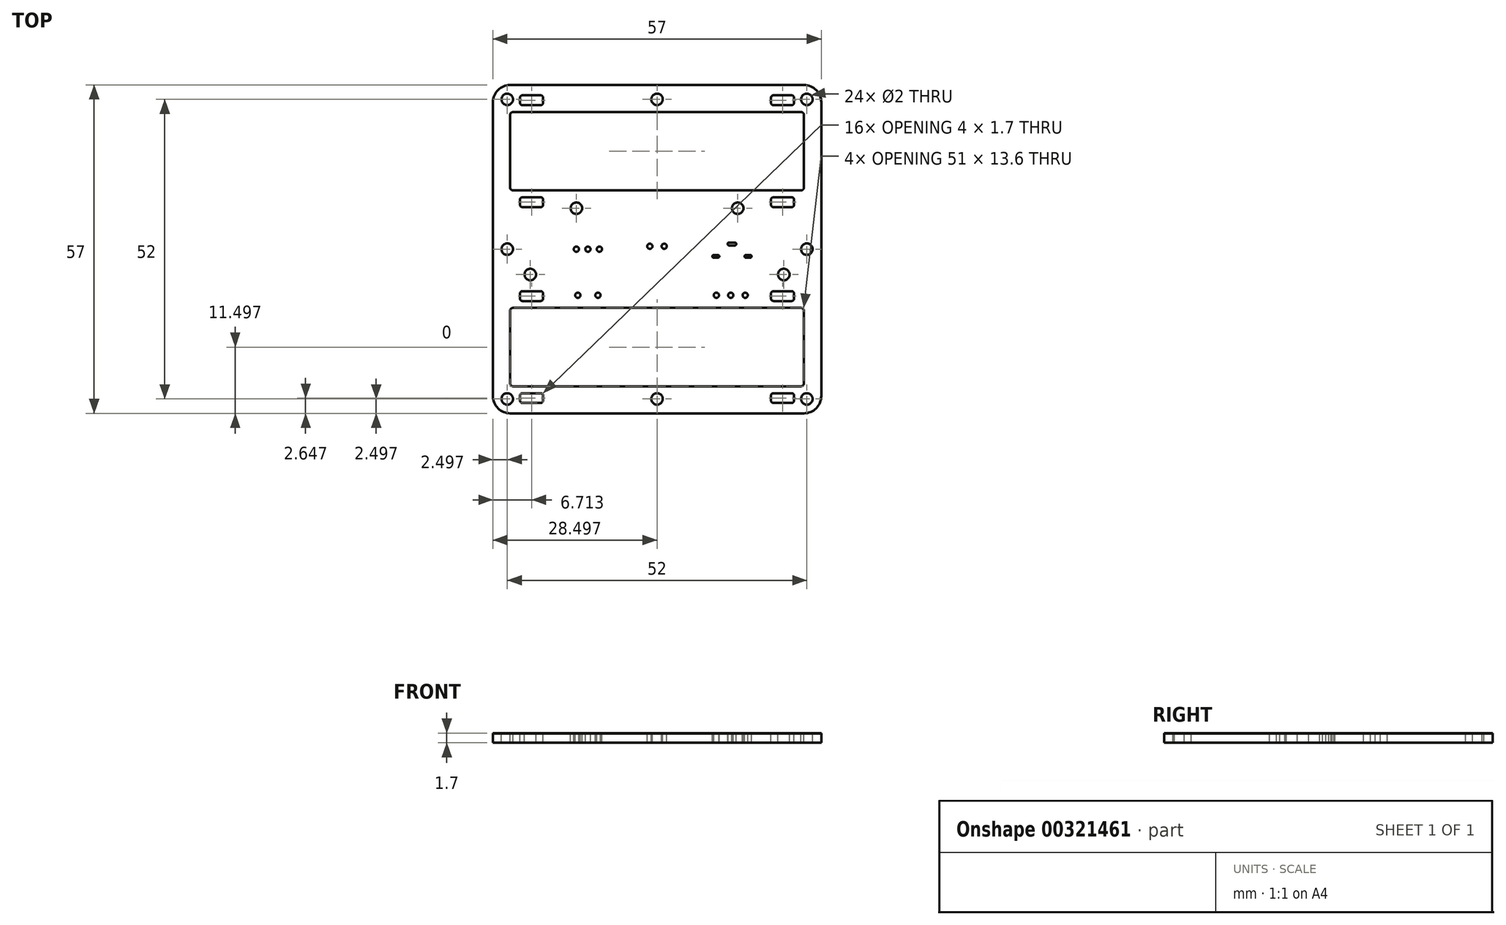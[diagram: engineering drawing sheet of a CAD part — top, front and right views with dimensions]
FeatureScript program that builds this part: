
annotation { "Feature Type Name" : "Feature", "Feature Type Description" : "" }
export const myFeature = defineFeature(function(context is Context, id is Id, definition is map)
    precondition{}
    {
        {
            var Q0;
            Q0=qCreatedBy(makeId("Top.planeOp"),FACE);
            var sketch = newSketch(context, id + "F0", { "sketchPlane" : qUnion([Q0])});
            skLineSegment(sketch, "E0.bottom", {"start": v(24.47, 58.7) * mm, "end": v(66.84, 58.7) * mm, "construction": true});
            skLineSegment(sketch, "E1.bottom", {"start": v(12.82, 58.7) * mm, "end": v(69.82, 58.7) * mm});
            skLineSegment(sketch, "E1.top", {"start": v(12.82, 1.7) * mm, "end": v(69.82, 1.7) * mm});
            skLineSegment(sketch, "E1.left", {"start": v(12.82, 58.7) * mm, "end": v(12.82, 1.7) * mm});
            skLineSegment(sketch, "E1.right", {"start": v(69.82, 58.7) * mm, "end": v(69.82, 1.7) * mm});
            skLineSegment(sketch, "E2", {"start": v(41.32, 58.7) * mm, "end": v(41.32, 1.7) * mm, "construction": true});
            skSolve(sketch);
        }
        {
            var Q0;
            Q0=qSketchRegion(id+"F0",true);
            extrude(context, id + "F1", {"entities" : qUnion([Q0]), "depth" : 1.6 * mm});
        }
        {
            var Q0;
            Q0=makeQuery(id+"F1.opExtrude","CAP_FACE",FACE,{"disambiguationData":[OSD([sQuery(id+"F0.wireOp",EDGE,"E1.bottom"),sQuery(id+"F0.wireOp",EDGE,"E1.top"),sQuery(id+"F0.wireOp",EDGE,"E1.left"),sQuery(id+"F0.wireOp",EDGE,"E1.right")])],"isStart":false});
            var sketch = newSketch(context, id + "F2", { "sketchPlane" : qUnion([Q0])});
            skCircle(sketch, "E3", {"center": v(27.32, 30.2) * mm, "radius": 0.45 * mm});
            skLineSegment(sketch, "E4", {"start": v(41.32, 22.32) * mm, "end": v(41.32, 29.29) * mm, "construction": true});
            skCircle(sketch, "E5.1.0.0", {"center": v(29.32, 30.2) * mm, "radius": 0.45 * mm});
            skLineSegment(sketch, "E5.direction1", {"start": v(27.32, 30.2) * mm, "end": v(29.32, 30.2) * mm, "construction": true});
            skCircle(sketch, "E6.0.2.0", {"center": v(31.32, 30.2) * mm, "radius": 0.45 * mm});
            skSolve(sketch);
        }
        {
            var Q0;
            Q0=makeQuery(id+"F1.opExtrude","CAP_FACE",FACE,{"disambiguationData":[OSD([sQuery(id+"F0.wireOp",EDGE,"E1.bottom"),sQuery(id+"F0.wireOp",EDGE,"E1.top"),sQuery(id+"F0.wireOp",EDGE,"E1.left"),sQuery(id+"F0.wireOp",EDGE,"E1.right")])],"isStart":false});
            var sketch = newSketch(context, id + "F3", { "sketchPlane" : qUnion([Q0])});
            skLineSegment(sketch, "E7", {"start": v(54.32, 14.1) * mm, "end": v(54.32, 27.42) * mm, "construction": true});
            skLineSegment(sketch, "E8", {"start": v(41.32, 6.29) * mm, "end": v(41.32, 24.04) * mm, "construction": true});
            skLineSegment(sketch, "E9", {"start": v(51.17, 28.95) * mm, "end": v(51.87, 28.95) * mm, "construction": true});
            skLineSegment(sketch, "E10", {"start": v(51.52, 23.97) * mm, "end": v(51.52, 28.95) * mm, "construction": true});
            skLineSegment(sketch, "E11", {"start": v(53.82, 31.1) * mm, "end": v(54.82, 31.1) * mm, "construction": true});
            skLineSegment(sketch, "E12", {"start": v(54.32, 31.1) * mm, "end": v(54.32, 19.92) * mm, "construction": true});
            skArc(sketch, "E13.0.startCap", {"start": v(53.82, 30.85) * mm, "mid": v(53.57, 31.1) * mm, "end": v(53.82, 31.35) * mm});
            skArc(sketch, "E13.0.endCap", {"start": v(54.82, 31.35) * mm, "mid": v(55.07, 31.1) * mm, "end": v(54.82, 30.85) * mm});
            skLineSegment(sketch, "E13.0.left", {"start": v(53.82, 31.35) * mm, "end": v(54.82, 31.35) * mm});
            skLineSegment(sketch, "E13.0.right", {"start": v(53.82, 30.85) * mm, "end": v(54.82, 30.85) * mm});
            skLineSegment(sketch, "E14", {"start": v(50.45, 30.1) * mm, "end": v(53.65, 30.1) * mm, "construction": true});
            skArc(sketch, "E15.0.startCap", {"start": v(51.87, 29.2) * mm, "mid": v(52.12, 28.95) * mm, "end": v(51.87, 28.7) * mm});
            skArc(sketch, "E15.0.endCap", {"start": v(51.17, 28.7) * mm, "mid": v(50.92, 28.95) * mm, "end": v(51.17, 29.2) * mm});
            skLineSegment(sketch, "E15.0.left", {"start": v(51.17, 28.7) * mm, "end": v(51.87, 28.7) * mm});
            skLineSegment(sketch, "E15.0.right", {"start": v(51.17, 29.2) * mm, "end": v(51.87, 29.2) * mm});
            skArc(sketch, "E16.MirrorCS", {"start": v(57.47, 28.7) * mm, "mid": v(57.72, 28.95) * mm, "end": v(57.47, 29.2) * mm});
            skLineSegment(sketch, "E17.MirrorCS", {"start": v(57.47, 28.7) * mm, "end": v(56.77, 28.7) * mm});
            skLineSegment(sketch, "E18.MirrorCS", {"start": v(57.47, 29.2) * mm, "end": v(56.77, 29.2) * mm});
            skArc(sketch, "E19.MirrorCS", {"start": v(56.77, 29.2) * mm, "mid": v(56.52, 28.95) * mm, "end": v(56.77, 28.7) * mm});
            skSolve(sketch);
        }
        {
            var Q0;
            Q0=makeQuery(id+"F1.opExtrude","CAP_FACE",FACE,{"disambiguationData":[OSD([sQuery(id+"F0.wireOp",EDGE,"E1.bottom"),sQuery(id+"F0.wireOp",EDGE,"E1.top"),sQuery(id+"F0.wireOp",EDGE,"E1.left"),sQuery(id+"F0.wireOp",EDGE,"E1.right")])],"isStart":false});
            var sketch = newSketch(context, id + "F4", { "sketchPlane" : qUnion([Q0])});
            skCircle(sketch, "E20", {"center": v(51.62, 22.2) * mm, "radius": 0.45 * mm});
            skCircle(sketch, "E21.1.0.0", {"center": v(56.62, 22.2) * mm, "radius": 0.45 * mm});
            skLineSegment(sketch, "E21.direction1", {"start": v(51.62, 22.2) * mm, "end": v(56.62, 22.2) * mm, "construction": true});
            skLineSegment(sketch, "E22", {"start": v(41.32, 6.29) * mm, "end": v(41.32, 17.65) * mm, "construction": true});
            skLineSegment(sketch, "E23", {"start": v(54.12, 22.2) * mm, "end": v(54.12, 23.7) * mm, "construction": true});
            skCircle(sketch, "E24", {"center": v(54.12, 22.2) * mm, "radius": 0.45 * mm});
            skSolve(sketch);
        }
        {
            var Q0;
            Q0=makeQuery(id+"F1.opExtrude","CAP_FACE",FACE,{"disambiguationData":[OSD([sQuery(id+"F0.wireOp",EDGE,"E1.bottom"),sQuery(id+"F0.wireOp",EDGE,"E1.top"),sQuery(id+"F0.wireOp",EDGE,"E1.left"),sQuery(id+"F0.wireOp",EDGE,"E1.right")])],"isStart":false});
            var sketch = newSketch(context, id + "F5", { "sketchPlane" : qUnion([Q0])});
            skCircle(sketch, "E25", {"center": v(40.07, 30.7) * mm, "radius": 0.45 * mm});
            skCircle(sketch, "E26.1.0.0", {"center": v(42.57, 30.7) * mm, "radius": 0.45 * mm});
            skLineSegment(sketch, "E26.direction1", {"start": v(40.07, 30.7) * mm, "end": v(42.57, 30.7) * mm, "construction": true});
            skLineSegment(sketch, "E27", {"start": v(41.32, 15.29) * mm, "end": v(41.32, 29.29) * mm, "construction": true});
            skLineSegment(sketch, "E28", {"start": v(41.32, 26.14) * mm, "end": v(41.32, 30.7) * mm, "construction": true});
            skSolve(sketch);
        }
        {
            var Q0;
            Q0=makeQuery(id+"F1.opExtrude","CAP_FACE",FACE,{"disambiguationData":[OSD([sQuery(id+"F0.wireOp",EDGE,"E1.bottom"),sQuery(id+"F0.wireOp",EDGE,"E1.top"),sQuery(id+"F0.wireOp",EDGE,"E1.left"),sQuery(id+"F0.wireOp",EDGE,"E1.right")])],"isStart":false});
            var sketch = newSketch(context, id + "F6", { "sketchPlane" : qUnion([Q0])});
            skCircle(sketch, "E29", {"center": v(27.57, 22.2) * mm, "radius": 0.45 * mm});
            skCircle(sketch, "E30.1.0.0", {"center": v(31.07, 22.2) * mm, "radius": 0.45 * mm});
            skLineSegment(sketch, "E30.direction1", {"start": v(27.57, 22.2) * mm, "end": v(31.07, 22.2) * mm, "construction": true});
            skLineSegment(sketch, "E31", {"start": v(29.32, 26.4) * mm, "end": v(29.32, 22.2) * mm, "construction": true});
            skSolve(sketch);
        }
        {
            var Q0;
            Q0=qSketchRegion(id+"F4",true);
            var Q1;
            Q1=qSketchRegion(id+"F5",true);
            var Q2;
            Q2=qSketchRegion(id+"F6",true);
            var Q3;
            Q3=qSketchRegion(id+"F3",true);
            var Q4;
            Q4=qSketchRegion(id+"F2",true);
            extrude(context, id + "F7", {"entities" : qUnion([Q0, Q1, Q2, Q3, Q4]), "operationType" : NewBodyOperationType.REMOVE, "oppositeDirection" : true, "depth" : 4 * mm});
        }
        {
            var Q0;
            Q0=makeQuery(id+"F1.opExtrude","SWEPT_EDGE",EDGE,{"disambiguationData":[OSD([sQuery(id+"F0.wireOp",EDGE,"E1.top"),sQuery(id+"F0.wireOp",EDGE,"E1.left")])]});
            var Q1;
            Q1=makeQuery(id+"F1.opExtrude","SWEPT_EDGE",EDGE,{"disambiguationData":[OSD([sQuery(id+"F0.wireOp",EDGE,"E1.top"),sQuery(id+"F0.wireOp",EDGE,"E1.right")])]});
            var Q2;
            Q2=makeQuery(id+"F1.opExtrude","SWEPT_EDGE",EDGE,{"disambiguationData":[OSD([sQuery(id+"F0.wireOp",EDGE,"E1.bottom"),sQuery(id+"F0.wireOp",EDGE,"E1.right")])]});
            var Q3;
            Q3=makeQuery(id+"F1.opExtrude","SWEPT_EDGE",EDGE,{"disambiguationData":[OSD([sQuery(id+"F0.wireOp",EDGE,"E1.bottom"),sQuery(id+"F0.wireOp",EDGE,"E1.left")])]});
            fillet(context, id + "F8", {"entities" : qUnion([Q0, Q1, Q2, Q3]), "radius" : 3 * mm, "tangentPropagation" : true, "allowEdgeOverflow" : false});
        }
        {
            var Q0;
            Q0=makeQuery(id+"F1.opExtrude","CAP_FACE",FACE,{"disambiguationData":[OSD([sQuery(id+"F0.wireOp",EDGE,"E1.bottom"),sQuery(id+"F0.wireOp",EDGE,"E1.top"),sQuery(id+"F0.wireOp",EDGE,"E1.left"),sQuery(id+"F0.wireOp",EDGE,"E1.right")])],"isStart":false});
            var sketch = newSketch(context, id + "F9", { "sketchPlane" : qUnion([Q0])});
            skLineSegment(sketch, "E32", {"start": v(41.32, 58.7) * mm, "end": v(41.32, 1.7) * mm, "construction": true});
            skLineSegment(sketch, "E33", {"start": v(12.82, 30.2) * mm, "end": v(69.82, 30.2) * mm, "construction": true});
            skCircle(sketch, "E34", {"center": v(63.32, 25.8) * mm, "radius": 1 * mm});
            skCircle(sketch, "E35.MirrorC", {"center": v(19.32, 25.8) * mm, "radius": 1 * mm});
            skCircle(sketch, "E36", {"center": v(55.32, 37.3) * mm, "radius": 1 * mm});
            skCircle(sketch, "E37.MirrorC", {"center": v(27.32, 37.3) * mm, "radius": 1 * mm});
            skCircle(sketch, "E38", {"center": v(15.32, 56.2) * mm, "radius": 1 * mm});
            skCircle(sketch, "E39.MirrorC", {"center": v(67.32, 56.2) * mm, "radius": 1 * mm});
            skCircle(sketch, "E40.MirrorC", {"center": v(15.32, 4.2) * mm, "radius": 1 * mm});
            skCircle(sketch, "E41.MirrorC", {"center": v(67.32, 4.2) * mm, "radius": 1 * mm});
            skCircle(sketch, "E42", {"center": v(41.32, 56.2) * mm, "radius": 1 * mm});
            skCircle(sketch, "E43.MirrorC", {"center": v(41.32, 4.2) * mm, "radius": 1 * mm});
            skCircle(sketch, "E44", {"center": v(15.32, 30.2) * mm, "radius": 1 * mm});
            skCircle(sketch, "E45", {"center": v(67.32, 30.2) * mm, "radius": 1 * mm});
            skSolve(sketch);
        }
        {
            var Q0;
            Q0=qSketchRegion(id+"F9",true);
            extrude(context, id + "F10", {"entities" : qUnion([Q0]), "operationType" : NewBodyOperationType.REMOVE, "oppositeDirection" : true, "depth" : 25 * mm});
        }
        {
            var Q0;
            Q0=makeQuery(id+"F1.opExtrude","CAP_FACE",FACE,{"disambiguationData":[OSD([sQuery(id+"F0.wireOp",EDGE,"E1.bottom"),sQuery(id+"F0.wireOp",EDGE,"E1.top"),sQuery(id+"F0.wireOp",EDGE,"E1.left"),sQuery(id+"F0.wireOp",EDGE,"E1.right")])],"isStart":false});
            var sketch = newSketch(context, id + "F11", { "sketchPlane" : qUnion([Q0])});
            skLineSegment(sketch, "E46", {"start": v(41.32, 58.7) * mm, "end": v(41.32, 1.7) * mm, "construction": true});
            skLineSegment(sketch, "E47.bottom", {"start": v(66.32, 20) * mm, "end": v(16.32, 20) * mm});
            skLineSegment(sketch, "E47.top", {"start": v(66.32, 6.4) * mm, "end": v(16.32, 6.4) * mm});
            skLineSegment(sketch, "E47.left", {"start": v(66.82, 19.5) * mm, "end": v(66.82, 6.9) * mm});
            skLineSegment(sketch, "E47.right", {"start": v(15.82, 19.5) * mm, "end": v(15.82, 6.9) * mm});
            skPoint(sketch, "E47.middle", {"position": v(41.32, 13.2) * mm});
            skLineSegment(sketch, "E48", {"start": v(41.32, 30.2) * mm, "end": v(-6.1, 30.2) * mm, "construction": true});
            skPoint(sketch, "E49.visualSharp", {"position": v(15.82, 6.4) * mm});
            skArc(sketch, "E49.filletArc", {"start": v(15.82, 6.9) * mm, "mid": v(15.96, 6.54) * mm, "end": v(16.32, 6.4) * mm});
            skPoint(sketch, "E50.visualSharp", {"position": v(15.82, 20) * mm});
            skArc(sketch, "E50.filletArc", {"start": v(16.32, 20) * mm, "mid": v(15.96, 19.85) * mm, "end": v(15.82, 19.5) * mm});
            skPoint(sketch, "E51.visualSharp", {"position": v(66.82, 20) * mm});
            skArc(sketch, "E51.filletArc", {"start": v(66.82, 19.5) * mm, "mid": v(66.67, 19.85) * mm, "end": v(66.32, 20) * mm});
            skPoint(sketch, "E52.visualSharp", {"position": v(66.82, 6.4) * mm});
            skArc(sketch, "E52.filletArc", {"start": v(66.32, 6.4) * mm, "mid": v(66.67, 6.54) * mm, "end": v(66.82, 6.9) * mm});
            skArc(sketch, "E53.MirrorCS", {"start": v(15.82, 53.5) * mm, "mid": v(15.96, 53.85) * mm, "end": v(16.32, 54) * mm});
            skArc(sketch, "E54.MirrorCS", {"start": v(16.32, 40.4) * mm, "mid": v(15.96, 40.54) * mm, "end": v(15.82, 40.9) * mm});
            skArc(sketch, "E55.MirrorCS", {"start": v(66.82, 40.9) * mm, "mid": v(66.67, 40.54) * mm, "end": v(66.32, 40.4) * mm});
            skArc(sketch, "E56.MirrorCS", {"start": v(66.32, 54) * mm, "mid": v(66.67, 53.85) * mm, "end": v(66.82, 53.5) * mm});
            skLineSegment(sketch, "E57.MirrorCS", {"start": v(15.82, 40.9) * mm, "end": v(15.82, 53.5) * mm});
            skLineSegment(sketch, "E58.MirrorCS", {"start": v(66.32, 40.4) * mm, "end": v(16.32, 40.4) * mm});
            skLineSegment(sketch, "E59.MirrorCS", {"start": v(66.82, 40.9) * mm, "end": v(66.82, 53.5) * mm});
            skLineSegment(sketch, "E60.MirrorCS", {"start": v(66.32, 54) * mm, "end": v(16.32, 54) * mm});
            skPoint(sketch, "E61.MirrorP", {"position": v(66.82, 54) * mm});
            skPoint(sketch, "E62.MirrorP", {"position": v(15.82, 54) * mm});
            skPoint(sketch, "E63.MirrorP", {"position": v(41.32, 47.2) * mm});
            skPoint(sketch, "E64.MirrorP", {"position": v(66.82, 40.4) * mm});
            skPoint(sketch, "E65.MirrorP", {"position": v(15.82, 40.4) * mm});
            skSolve(sketch);
        }
        {
            var Q0;
            Q0=qSketchRegion(id+"F11",true);
            extrude(context, id + "F12", {"entities" : qUnion([Q0]), "operationType" : NewBodyOperationType.REMOVE, "oppositeDirection" : true, "depth" : 5 * mm});
        }
        {
            var Q0;
            Q0=makeQuery(id+"F1.opExtrude","CAP_FACE",FACE,{"disambiguationData":[OSD([sQuery(id+"F0.wireOp",EDGE,"E1.bottom"),sQuery(id+"F0.wireOp",EDGE,"E1.top"),sQuery(id+"F0.wireOp",EDGE,"E1.left"),sQuery(id+"F0.wireOp",EDGE,"E1.right")])],"isStart":false});
            var sketch = newSketch(context, id + "F13", { "sketchPlane" : qUnion([Q0])});
            skLineSegment(sketch, "E66.bottom", {"start": v(17.53, 5.2) * mm, "end": v(21.53, 5.2) * mm});
            skLineSegment(sketch, "E66.top", {"start": v(17.53, 3.5) * mm, "end": v(21.53, 3.5) * mm});
            skLineSegment(sketch, "E66.left", {"start": v(17.53, 5.2) * mm, "end": v(17.53, 3.5) * mm});
            skLineSegment(sketch, "E66.right", {"start": v(21.53, 5.2) * mm, "end": v(21.53, 3.5) * mm});
            skLineSegment(sketch, "E67.MirrorCS", {"start": v(65.1, 5.2) * mm, "end": v(65.1, 3.5) * mm});
            skLineSegment(sketch, "E68.MirrorCS", {"start": v(61.1, 5.2) * mm, "end": v(61.1, 3.5) * mm});
            skLineSegment(sketch, "E69.MirrorCS", {"start": v(65.1, 3.5) * mm, "end": v(61.1, 3.5) * mm});
            skLineSegment(sketch, "E70.MirrorCS", {"start": v(65.1, 5.2) * mm, "end": v(61.1, 5.2) * mm});
            skLineSegment(sketch, "E71", {"start": v(12.82, 30.2) * mm, "end": v(83.5, 30.2) * mm, "construction": true});
            skLineSegment(sketch, "E72", {"start": v(15.82, 13.2) * mm, "end": v(-2.11, 13.2) * mm, "construction": true});
            skPoint(sketch, "E72.endSnap0", {"position": v(15.82, 13.2) * mm});
            skLineSegment(sketch, "E73.MirrorCS", {"start": v(61.1, 21.2) * mm, "end": v(61.1, 22.9) * mm});
            skLineSegment(sketch, "E74.MirrorCS", {"start": v(65.1, 21.2) * mm, "end": v(65.1, 22.9) * mm});
            skLineSegment(sketch, "E75.MirrorCS", {"start": v(21.53, 21.2) * mm, "end": v(21.53, 22.9) * mm});
            skLineSegment(sketch, "E76.MirrorCS", {"start": v(17.53, 21.2) * mm, "end": v(17.53, 22.9) * mm});
            skLineSegment(sketch, "E77.MirrorCS", {"start": v(65.1, 21.2) * mm, "end": v(61.1, 21.2) * mm});
            skLineSegment(sketch, "E78.MirrorCS", {"start": v(65.1, 22.9) * mm, "end": v(61.1, 22.9) * mm});
            skLineSegment(sketch, "E79.MirrorCS", {"start": v(17.53, 22.9) * mm, "end": v(21.53, 22.9) * mm});
            skLineSegment(sketch, "E80.MirrorCS", {"start": v(17.53, 21.2) * mm, "end": v(21.53, 21.2) * mm});
            skLineSegment(sketch, "E81.MirrorCS", {"start": v(17.53, 39.2) * mm, "end": v(17.53, 37.5) * mm});
            skLineSegment(sketch, "E82.MirrorCS", {"start": v(17.53, 55.2) * mm, "end": v(17.53, 56.9) * mm});
            skLineSegment(sketch, "E83.MirrorCS", {"start": v(61.1, 39.2) * mm, "end": v(61.1, 37.5) * mm});
            skLineSegment(sketch, "E84.MirrorCS", {"start": v(21.53, 55.2) * mm, "end": v(21.53, 56.9) * mm});
            skLineSegment(sketch, "E85.MirrorCS", {"start": v(65.1, 55.2) * mm, "end": v(65.1, 56.9) * mm});
            skLineSegment(sketch, "E86.MirrorCS", {"start": v(21.53, 39.2) * mm, "end": v(21.53, 37.5) * mm});
            skLineSegment(sketch, "E87.MirrorCS", {"start": v(61.1, 55.2) * mm, "end": v(61.1, 56.9) * mm});
            skLineSegment(sketch, "E88.MirrorCS", {"start": v(65.1, 39.2) * mm, "end": v(65.1, 37.5) * mm});
            skLineSegment(sketch, "E89.MirrorCS", {"start": v(17.53, 56.9) * mm, "end": v(21.53, 56.9) * mm});
            skLineSegment(sketch, "E90.MirrorCS", {"start": v(65.1, 39.2) * mm, "end": v(61.1, 39.2) * mm});
            skLineSegment(sketch, "E91.MirrorCS", {"start": v(65.1, 37.5) * mm, "end": v(61.1, 37.5) * mm});
            skLineSegment(sketch, "E92.MirrorCS", {"start": v(17.53, 39.2) * mm, "end": v(21.53, 39.2) * mm});
            skLineSegment(sketch, "E93.MirrorCS", {"start": v(17.53, 55.2) * mm, "end": v(21.53, 55.2) * mm});
            skLineSegment(sketch, "E94.MirrorCS", {"start": v(65.1, 56.9) * mm, "end": v(61.1, 56.9) * mm});
            skPoint(sketch, "E95.MirrorP", {"position": v(15.82, 47.2) * mm});
            skLineSegment(sketch, "E96.MirrorCS", {"start": v(65.1, 55.2) * mm, "end": v(61.1, 55.2) * mm});
            skLineSegment(sketch, "E97.MirrorCS", {"start": v(17.53, 37.5) * mm, "end": v(21.53, 37.5) * mm});
            skSolve(sketch);
        }
        {
            var Q0;
            Q0=qSketchRegion(id+"F13",true);
            extrude(context, id + "F14", {"entities" : qUnion([Q0]), "operationType" : NewBodyOperationType.REMOVE, "oppositeDirection" : true, "depth" : 25 * mm});
        }
        {
            var Q0;
            Q0=makeQuery(id+"F14.boolean.opBoolean","COPY",EDGE,{"derivedFrom":makeQuery(id+"F14.opExtrude","SWEPT_EDGE",EDGE,{"disambiguationData":[OSD([sQuery(id+"F13.wireOp",EDGE,"E82.MirrorCS"),sQuery(id+"F13.wireOp",EDGE,"E89.MirrorCS")])]})});
            var Q1;
            Q1=makeQuery(id+"F14.boolean.opBoolean","COPY",EDGE,{"derivedFrom":makeQuery(id+"F14.opExtrude","SWEPT_EDGE",EDGE,{"disambiguationData":[OSD([sQuery(id+"F13.wireOp",EDGE,"E82.MirrorCS"),sQuery(id+"F13.wireOp",EDGE,"E93.MirrorCS")])]})});
            var Q2;
            Q2=makeQuery(id+"F14.boolean.opBoolean","COPY",EDGE,{"derivedFrom":makeQuery(id+"F14.opExtrude","SWEPT_EDGE",EDGE,{"disambiguationData":[OSD([sQuery(id+"F13.wireOp",EDGE,"E84.MirrorCS"),sQuery(id+"F13.wireOp",EDGE,"E93.MirrorCS")])]})});
            var Q3;
            Q3=makeQuery(id+"F14.boolean.opBoolean","COPY",EDGE,{"derivedFrom":makeQuery(id+"F14.opExtrude","SWEPT_EDGE",EDGE,{"disambiguationData":[OSD([sQuery(id+"F13.wireOp",EDGE,"E84.MirrorCS"),sQuery(id+"F13.wireOp",EDGE,"E89.MirrorCS")])]})});
            var Q4;
            Q4=makeQuery(id+"F14.boolean.opBoolean","COPY",EDGE,{"derivedFrom":makeQuery(id+"F14.opExtrude","SWEPT_EDGE",EDGE,{"disambiguationData":[OSD([sQuery(id+"F13.wireOp",EDGE,"E86.MirrorCS"),sQuery(id+"F13.wireOp",EDGE,"E92.MirrorCS")])]})});
            var Q5;
            Q5=makeQuery(id+"F14.boolean.opBoolean","COPY",EDGE,{"derivedFrom":makeQuery(id+"F14.opExtrude","SWEPT_EDGE",EDGE,{"disambiguationData":[OSD([sQuery(id+"F13.wireOp",EDGE,"E81.MirrorCS"),sQuery(id+"F13.wireOp",EDGE,"E92.MirrorCS")])]})});
            var Q6;
            Q6=makeQuery(id+"F14.boolean.opBoolean","COPY",EDGE,{"derivedFrom":makeQuery(id+"F14.opExtrude","SWEPT_EDGE",EDGE,{"disambiguationData":[OSD([sQuery(id+"F13.wireOp",EDGE,"E81.MirrorCS"),sQuery(id+"F13.wireOp",EDGE,"E97.MirrorCS")])]})});
            var Q7;
            Q7=makeQuery(id+"F14.boolean.opBoolean","COPY",EDGE,{"derivedFrom":makeQuery(id+"F14.opExtrude","SWEPT_EDGE",EDGE,{"disambiguationData":[OSD([sQuery(id+"F13.wireOp",EDGE,"E86.MirrorCS"),sQuery(id+"F13.wireOp",EDGE,"E97.MirrorCS")])]})});
            var Q8;
            Q8=makeQuery(id+"F14.boolean.opBoolean","COPY",EDGE,{"derivedFrom":makeQuery(id+"F14.opExtrude","SWEPT_EDGE",EDGE,{"disambiguationData":[OSD([sQuery(id+"F13.wireOp",EDGE,"E85.MirrorCS"),sQuery(id+"F13.wireOp",EDGE,"E96.MirrorCS")])]})});
            var Q9;
            Q9=makeQuery(id+"F14.boolean.opBoolean","COPY",EDGE,{"derivedFrom":makeQuery(id+"F14.opExtrude","SWEPT_EDGE",EDGE,{"disambiguationData":[OSD([sQuery(id+"F13.wireOp",EDGE,"E85.MirrorCS"),sQuery(id+"F13.wireOp",EDGE,"E94.MirrorCS")])]})});
            var Q10;
            Q10=makeQuery(id+"F14.boolean.opBoolean","COPY",EDGE,{"derivedFrom":makeQuery(id+"F14.opExtrude","SWEPT_EDGE",EDGE,{"disambiguationData":[OSD([sQuery(id+"F13.wireOp",EDGE,"E87.MirrorCS"),sQuery(id+"F13.wireOp",EDGE,"E94.MirrorCS")])]})});
            var Q11;
            Q11=makeQuery(id+"F14.boolean.opBoolean","COPY",EDGE,{"derivedFrom":makeQuery(id+"F14.opExtrude","SWEPT_EDGE",EDGE,{"disambiguationData":[OSD([sQuery(id+"F13.wireOp",EDGE,"E87.MirrorCS"),sQuery(id+"F13.wireOp",EDGE,"E96.MirrorCS")])]})});
            var Q12;
            Q12=makeQuery(id+"F14.boolean.opBoolean","COPY",EDGE,{"derivedFrom":makeQuery(id+"F14.opExtrude","SWEPT_EDGE",EDGE,{"disambiguationData":[OSD([sQuery(id+"F13.wireOp",EDGE,"E83.MirrorCS"),sQuery(id+"F13.wireOp",EDGE,"E91.MirrorCS")])]})});
            var Q13;
            Q13=makeQuery(id+"F14.boolean.opBoolean","COPY",EDGE,{"derivedFrom":makeQuery(id+"F14.opExtrude","SWEPT_EDGE",EDGE,{"disambiguationData":[OSD([sQuery(id+"F13.wireOp",EDGE,"E83.MirrorCS"),sQuery(id+"F13.wireOp",EDGE,"E90.MirrorCS")])]})});
            var Q14;
            Q14=makeQuery(id+"F14.boolean.opBoolean","COPY",EDGE,{"derivedFrom":makeQuery(id+"F14.opExtrude","SWEPT_EDGE",EDGE,{"disambiguationData":[OSD([sQuery(id+"F13.wireOp",EDGE,"E88.MirrorCS"),sQuery(id+"F13.wireOp",EDGE,"E90.MirrorCS")])]})});
            var Q15;
            Q15=makeQuery(id+"F14.boolean.opBoolean","COPY",EDGE,{"derivedFrom":makeQuery(id+"F14.opExtrude","SWEPT_EDGE",EDGE,{"disambiguationData":[OSD([sQuery(id+"F13.wireOp",EDGE,"E88.MirrorCS"),sQuery(id+"F13.wireOp",EDGE,"E91.MirrorCS")])]})});
            var Q16;
            Q16=makeQuery(id+"F14.boolean.opBoolean","COPY",EDGE,{"derivedFrom":makeQuery(id+"F14.opExtrude","SWEPT_EDGE",EDGE,{"disambiguationData":[OSD([sQuery(id+"F13.wireOp",EDGE,"E75.MirrorCS"),sQuery(id+"F13.wireOp",EDGE,"E80.MirrorCS")])]})});
            var Q17;
            Q17=makeQuery(id+"F14.boolean.opBoolean","COPY",EDGE,{"derivedFrom":makeQuery(id+"F14.opExtrude","SWEPT_EDGE",EDGE,{"disambiguationData":[OSD([sQuery(id+"F13.wireOp",EDGE,"E75.MirrorCS"),sQuery(id+"F13.wireOp",EDGE,"E79.MirrorCS")])]})});
            var Q18;
            Q18=makeQuery(id+"F14.boolean.opBoolean","COPY",EDGE,{"derivedFrom":makeQuery(id+"F14.opExtrude","SWEPT_EDGE",EDGE,{"disambiguationData":[OSD([sQuery(id+"F13.wireOp",EDGE,"E76.MirrorCS"),sQuery(id+"F13.wireOp",EDGE,"E79.MirrorCS")])]})});
            var Q19;
            Q19=makeQuery(id+"F14.boolean.opBoolean","COPY",EDGE,{"derivedFrom":makeQuery(id+"F14.opExtrude","SWEPT_EDGE",EDGE,{"disambiguationData":[OSD([sQuery(id+"F13.wireOp",EDGE,"E76.MirrorCS"),sQuery(id+"F13.wireOp",EDGE,"E80.MirrorCS")])]})});
            var Q20;
            Q20=makeQuery(id+"F14.boolean.opBoolean","COPY",EDGE,{"derivedFrom":makeQuery(id+"F14.opExtrude","SWEPT_EDGE",EDGE,{"disambiguationData":[OSD([sQuery(id+"F13.wireOp",EDGE,"E73.MirrorCS"),sQuery(id+"F13.wireOp",EDGE,"E77.MirrorCS")])]})});
            var Q21;
            Q21=makeQuery(id+"F14.boolean.opBoolean","COPY",EDGE,{"derivedFrom":makeQuery(id+"F14.opExtrude","SWEPT_EDGE",EDGE,{"disambiguationData":[OSD([sQuery(id+"F13.wireOp",EDGE,"E73.MirrorCS"),sQuery(id+"F13.wireOp",EDGE,"E78.MirrorCS")])]})});
            var Q22;
            Q22=makeQuery(id+"F14.boolean.opBoolean","COPY",EDGE,{"derivedFrom":makeQuery(id+"F14.opExtrude","SWEPT_EDGE",EDGE,{"disambiguationData":[OSD([sQuery(id+"F13.wireOp",EDGE,"E74.MirrorCS"),sQuery(id+"F13.wireOp",EDGE,"E78.MirrorCS")])]})});
            var Q23;
            Q23=makeQuery(id+"F14.boolean.opBoolean","COPY",EDGE,{"derivedFrom":makeQuery(id+"F14.opExtrude","SWEPT_EDGE",EDGE,{"disambiguationData":[OSD([sQuery(id+"F13.wireOp",EDGE,"E74.MirrorCS"),sQuery(id+"F13.wireOp",EDGE,"E77.MirrorCS")])]})});
            var Q24;
            Q24=makeQuery(id+"F14.boolean.opBoolean","COPY",EDGE,{"derivedFrom":makeQuery(id+"F14.opExtrude","SWEPT_EDGE",EDGE,{"disambiguationData":[OSD([sQuery(id+"F13.wireOp",EDGE,"E67.MirrorCS"),sQuery(id+"F13.wireOp",EDGE,"E69.MirrorCS")])]})});
            var Q25;
            Q25=makeQuery(id+"F14.boolean.opBoolean","COPY",EDGE,{"derivedFrom":makeQuery(id+"F14.opExtrude","SWEPT_EDGE",EDGE,{"disambiguationData":[OSD([sQuery(id+"F13.wireOp",EDGE,"E67.MirrorCS"),sQuery(id+"F13.wireOp",EDGE,"E70.MirrorCS")])]})});
            var Q26;
            Q26=makeQuery(id+"F14.boolean.opBoolean","COPY",EDGE,{"derivedFrom":makeQuery(id+"F14.opExtrude","SWEPT_EDGE",EDGE,{"disambiguationData":[OSD([sQuery(id+"F13.wireOp",EDGE,"E68.MirrorCS"),sQuery(id+"F13.wireOp",EDGE,"E70.MirrorCS")])]})});
            var Q27;
            Q27=makeQuery(id+"F14.boolean.opBoolean","COPY",EDGE,{"derivedFrom":makeQuery(id+"F14.opExtrude","SWEPT_EDGE",EDGE,{"disambiguationData":[OSD([sQuery(id+"F13.wireOp",EDGE,"E68.MirrorCS"),sQuery(id+"F13.wireOp",EDGE,"E69.MirrorCS")])]})});
            var Q28;
            Q28=makeQuery(id+"F14.boolean.opBoolean","COPY",EDGE,{"derivedFrom":makeQuery(id+"F14.opExtrude","SWEPT_EDGE",EDGE,{"disambiguationData":[OSD([sQuery(id+"F13.wireOp",EDGE,"E66.top"),sQuery(id+"F13.wireOp",EDGE,"E66.left")])]})});
            var Q29;
            Q29=makeQuery(id+"F14.boolean.opBoolean","COPY",EDGE,{"derivedFrom":makeQuery(id+"F14.opExtrude","SWEPT_EDGE",EDGE,{"disambiguationData":[OSD([sQuery(id+"F13.wireOp",EDGE,"E66.top"),sQuery(id+"F13.wireOp",EDGE,"E66.right")])]})});
            var Q30;
            Q30=makeQuery(id+"F14.boolean.opBoolean","COPY",EDGE,{"derivedFrom":makeQuery(id+"F14.opExtrude","SWEPT_EDGE",EDGE,{"disambiguationData":[OSD([sQuery(id+"F13.wireOp",EDGE,"E66.bottom"),sQuery(id+"F13.wireOp",EDGE,"E66.right")])]})});
            var Q31;
            Q31=makeQuery(id+"F14.boolean.opBoolean","COPY",EDGE,{"derivedFrom":makeQuery(id+"F14.opExtrude","SWEPT_EDGE",EDGE,{"disambiguationData":[OSD([sQuery(id+"F13.wireOp",EDGE,"E66.bottom"),sQuery(id+"F13.wireOp",EDGE,"E66.left")])]})});
            fillet(context, id + "F15", {"entities" : qUnion([Q0, Q1, Q2, Q3, Q4, Q5, Q6, Q7, Q8, Q9, Q10, Q11, Q12, Q13, Q14, Q15, Q16, Q17, Q18, Q19, Q20, Q21, Q22, Q23, Q24, Q25, Q26, Q27, Q28, Q29, Q30, Q31]), "radius" : .4 * mm, "tangentPropagation" : true, "allowEdgeOverflow" : false});
        }
        {
            var Q0;
            Q0=makeQuery(id+"F1.opExtrude","CAP_FACE",FACE,{"disambiguationData":[OSD([sQuery(id+"F0.wireOp",EDGE,"E1.bottom"),sQuery(id+"F0.wireOp",EDGE,"E1.top"),sQuery(id+"F0.wireOp",EDGE,"E1.left"),sQuery(id+"F0.wireOp",EDGE,"E1.right")])],"isStart":false});
            extrude(context, id + "F16", {"entities" : qUnion([Q0]), "depth" : .1 * mm});
        }
    });
